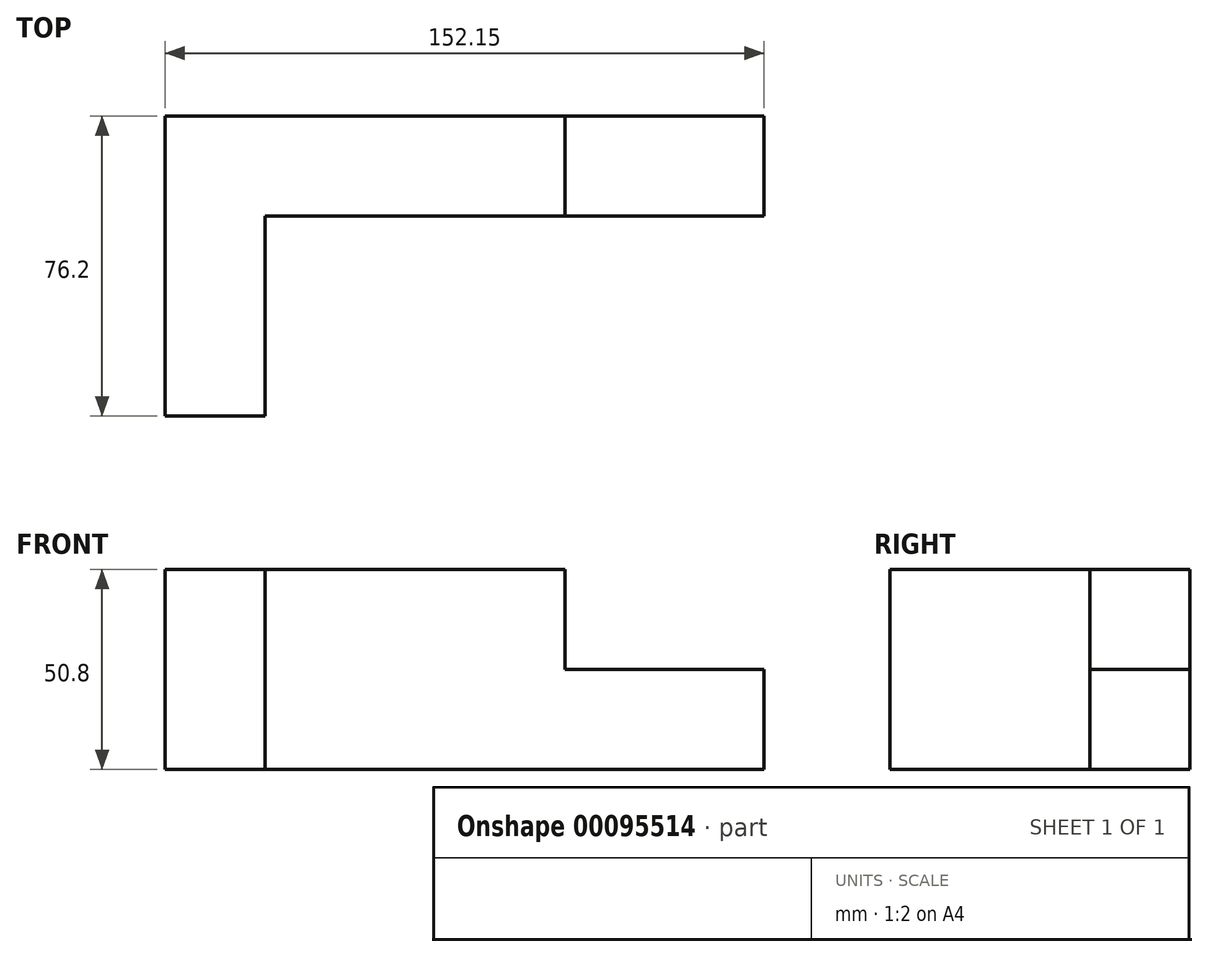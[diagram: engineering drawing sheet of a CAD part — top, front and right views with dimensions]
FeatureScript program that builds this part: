
annotation { "Feature Type Name" : "Feature", "Feature Type Description" : "" }
export const myFeature = defineFeature(function(context is Context, id is Id, definition is map)
    precondition{}
    {
        {
            var Q0;
            Q0=qCreatedBy(makeId("Top.planeOp"),FACE);
            var sketch = newSketch(context, id + "F0", { "sketchPlane" : qUnion([Q0])});
            skLineSegment(sketch, "E0.bottom", {"start": v(0, 0) * mm, "end": v(-25.4, 0) * mm});
            skLineSegment(sketch, "E0.top", {"start": v(0, -50.8) * mm, "end": v(-25.4, -50.8) * mm});
            skLineSegment(sketch, "E0.left", {"start": v(0, 0) * mm, "end": v(0, -50.8) * mm});
            skLineSegment(sketch, "E0.right", {"start": v(-25.4, 0) * mm, "end": v(-25.4, -50.8) * mm});
            skSolve(sketch);
        }
        {
            var Q0;
            Q0=qCreatedBy(makeId("Top.planeOp"),FACE);
            var sketch = newSketch(context, id + "F1", { "sketchPlane" : qUnion([Q0])});
            skLineSegment(sketch, "E1.bottom", {"start": v(0, 0) * mm, "end": v(-25.4, 0) * mm});
            skLineSegment(sketch, "E1.top", {"start": v(0, 25.4) * mm, "end": v(-25.4, 25.4) * mm});
            skLineSegment(sketch, "E1.left", {"start": v(0, 0) * mm, "end": v(0, 25.4) * mm});
            skLineSegment(sketch, "E1.right", {"start": v(-25.4, 0) * mm, "end": v(-25.4, 25.4) * mm});
            skSolve(sketch);
        }
        {
            var Q0;
            Q0=qCreatedBy(makeId("Top.planeOp"),FACE);
            var sketch = newSketch(context, id + "F2", { "sketchPlane" : qUnion([Q0])});
            skLineSegment(sketch, "E2.bottom", {"start": v(0, 0) * mm, "end": v(76.2, 0) * mm});
            skLineSegment(sketch, "E2.top", {"start": v(0, 25.4) * mm, "end": v(76.2, 25.4) * mm});
            skLineSegment(sketch, "E2.left", {"start": v(0, 0) * mm, "end": v(0, 25.4) * mm});
            skLineSegment(sketch, "E2.right", {"start": v(76.2, 0) * mm, "end": v(76.2, 25.4) * mm});
            skSolve(sketch);
        }
        {
            var Q0;
            Q0=makeQuery(id+"F0.imprint","IMPRINT",FACE,{"disambiguationData":[TD([[makeQuery(id+"F0.imprint","IMPRINT",EDGE,{"derivedFrom":sQuery(id+"F0.wireOp",EDGE,"E0.bottom")}),1.0]])]});
            extrude(context, id + "F3", {"entities" : qUnion([Q0]), "depth" : 50.8 * mm});
        }
        {
            var Q0;
            Q0=makeQuery(id+"F1.imprint","IMPRINT",FACE,{"disambiguationData":[TD([[makeQuery(id+"F1.imprint","IMPRINT",EDGE,{"derivedFrom":sQuery(id+"F1.wireOp",EDGE,"E1.bottom")}),-1.0]])]});
            extrude(context, id + "F4", {"entities" : qUnion([Q0]), "operationType" : NewBodyOperationType.ADD, "depth" : 50.8 * mm});
        }
        {
            var Q0;
            Q0=makeQuery(id+"F2.imprint","IMPRINT",FACE,{"disambiguationData":[TD([[makeQuery(id+"F2.imprint","IMPRINT",EDGE,{"derivedFrom":sQuery(id+"F2.wireOp",EDGE,"E2.bottom")}),1.0]])]});
            extrude(context, id + "F5", {"entities" : qUnion([Q0]), "operationType" : NewBodyOperationType.ADD, "depth" : 25.4 * mm});
        }
        {
            var Q0;
            Q0=makeQuery(id+"F5.opExtrude","CAP_FACE",FACE,{"disambiguationData":[OSD([sQuery(id+"F2.wireOp",EDGE,"E2.bottom"),sQuery(id+"F2.wireOp",EDGE,"E2.top"),sQuery(id+"F2.wireOp",EDGE,"E2.left"),sQuery(id+"F2.wireOp",EDGE,"E2.right")])],"isStart":false});
            extrude(context, id + "F6", {"entities" : qUnion([Q0]), "operationType" : NewBodyOperationType.ADD, "depth" : 25.4 * mm});
        }
        {
            var Q0;
            Q0=qCreatedBy(makeId("Top.planeOp"),FACE);
            var sketch = newSketch(context, id + "F7", { "sketchPlane" : qUnion([Q0])});
            skLineSegment(sketch, "E3.bottom", {"start": v(75.95, 0) * mm, "end": v(126.75, 0) * mm});
            skLineSegment(sketch, "E3.top", {"start": v(75.95, 25.4) * mm, "end": v(126.75, 25.4) * mm});
            skLineSegment(sketch, "E3.left", {"start": v(75.95, 0) * mm, "end": v(75.95, 25.4) * mm});
            skLineSegment(sketch, "E3.right", {"start": v(126.75, 0) * mm, "end": v(126.75, 25.4) * mm});
            skSolve(sketch);
        }
        {
            var Q0;
            Q0=makeQuery(id+"F7.imprint","IMPRINT",FACE,{"disambiguationData":[TD([[makeQuery(id+"F7.imprint","IMPRINT",EDGE,{"derivedFrom":sQuery(id+"F7.wireOp",EDGE,"E3.bottom")}),1.0]])]});
            extrude(context, id + "F8", {"entities" : qUnion([Q0]), "operationType" : NewBodyOperationType.ADD, "depth" : 25.4 * mm});
        }
    });
